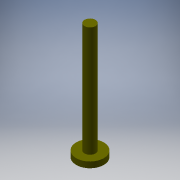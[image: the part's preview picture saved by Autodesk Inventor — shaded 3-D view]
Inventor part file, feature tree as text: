
AUTODESK INVENTOR PART (.ipt)
format: ipt  version: 2019 (Build 230136000, 136)  size: 111,616 bytes
history: native  units: mm
features: extrude x2, sketch x2
ambient origin geometry x8: Origin, YZ Plane, XZ Plane, XY Plane, X Axis, Y Axis, Z Axis, Center Point
bodies: Solid1 (feature_tree)
feature tree (4):
  extrude  "Extrusion1"  Depth=60.0mm TaperAngle=0.0deg
  extrude  "Extrusion2"  Depth=3.18mm TaperAngle=0.0deg
  sketch  "Sketch1"  dims[d0=6.0mm d1=60.0mm d2=0.0mm]
  sketch  "Sketch2"  dims[d3=15.0mm d4=3.18mm d5=0.0mm]
